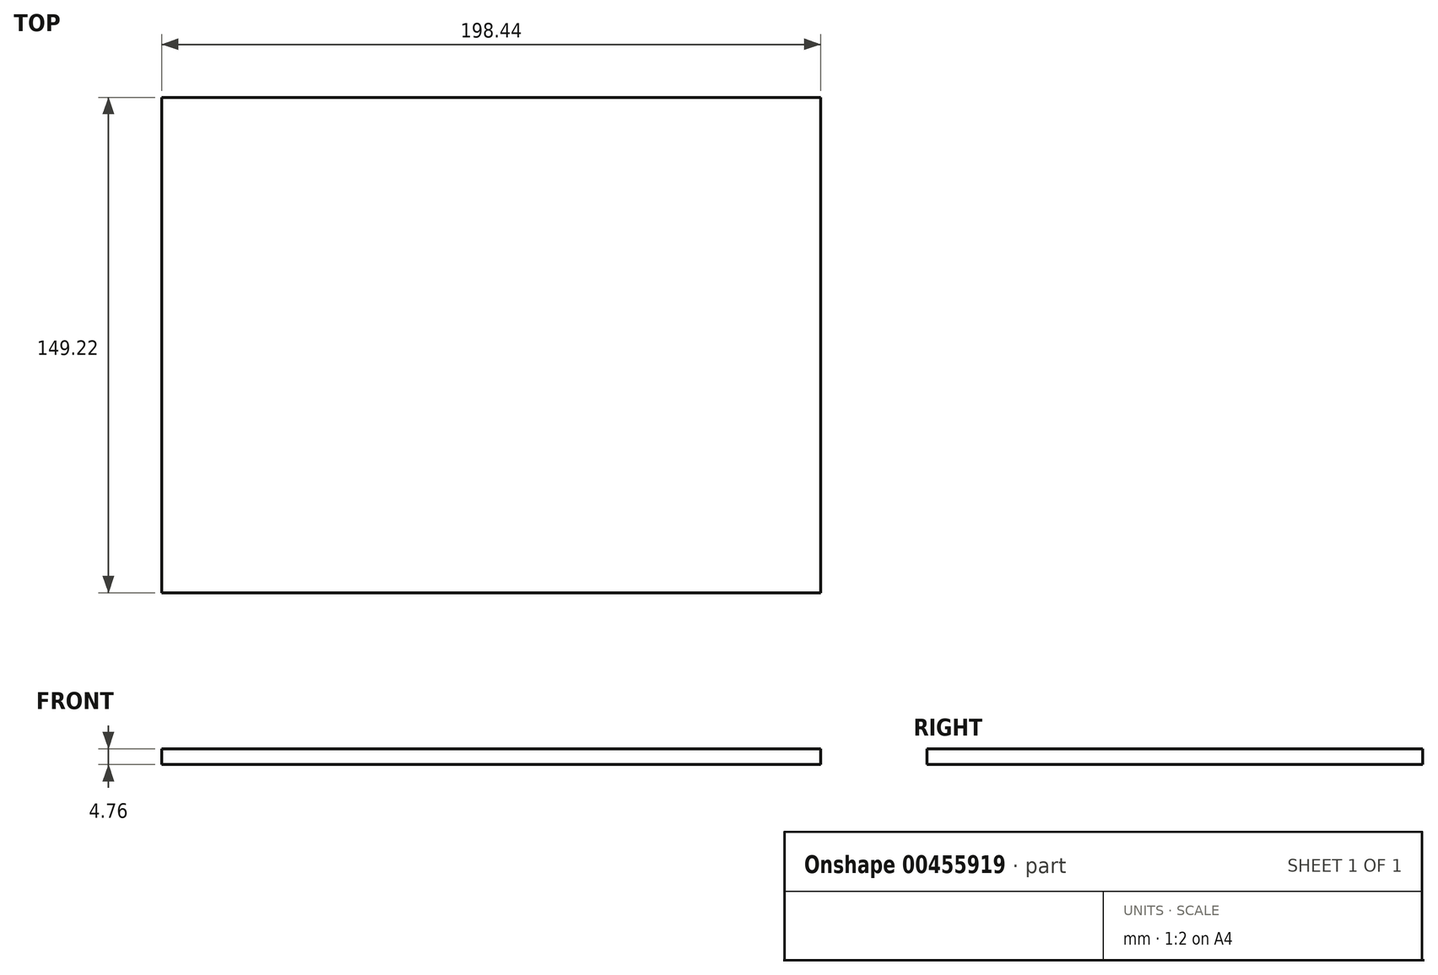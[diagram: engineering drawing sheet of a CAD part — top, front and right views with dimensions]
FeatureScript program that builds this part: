
annotation { "Feature Type Name" : "Feature", "Feature Type Description" : "" }
export const myFeature = defineFeature(function(context is Context, id is Id, definition is map)
    precondition{}
    {
        {
            var Q0;
            Q0=qCreatedBy(makeId("Top.planeOp"),FACE);
            var sketch = newSketch(context, id + "F0", { "sketchPlane" : qUnion([Q0])});
            skLineSegment(sketch, "E0.bottom", {"start": v(-99.22, 74.61) * mm, "end": v(99.22, 74.61) * mm});
            skLineSegment(sketch, "E0.top", {"start": v(-99.22, -74.61) * mm, "end": v(99.22, -74.61) * mm});
            skLineSegment(sketch, "E0.left", {"start": v(-99.22, 74.61) * mm, "end": v(-99.22, -74.61) * mm});
            skLineSegment(sketch, "E0.right", {"start": v(99.22, 74.61) * mm, "end": v(99.22, -74.61) * mm});
            skPoint(sketch, "E0.middle", {"position": v(0, 0) * mm});
            skSolve(sketch);
        }
        {
            var Q0;
            Q0 = qSketchRegion(id + "F0", true);
            extrude(context, id + "F1", {"entities" : qUnion([Q0]), "depth" : 4.76 * mm});
        }
    });
